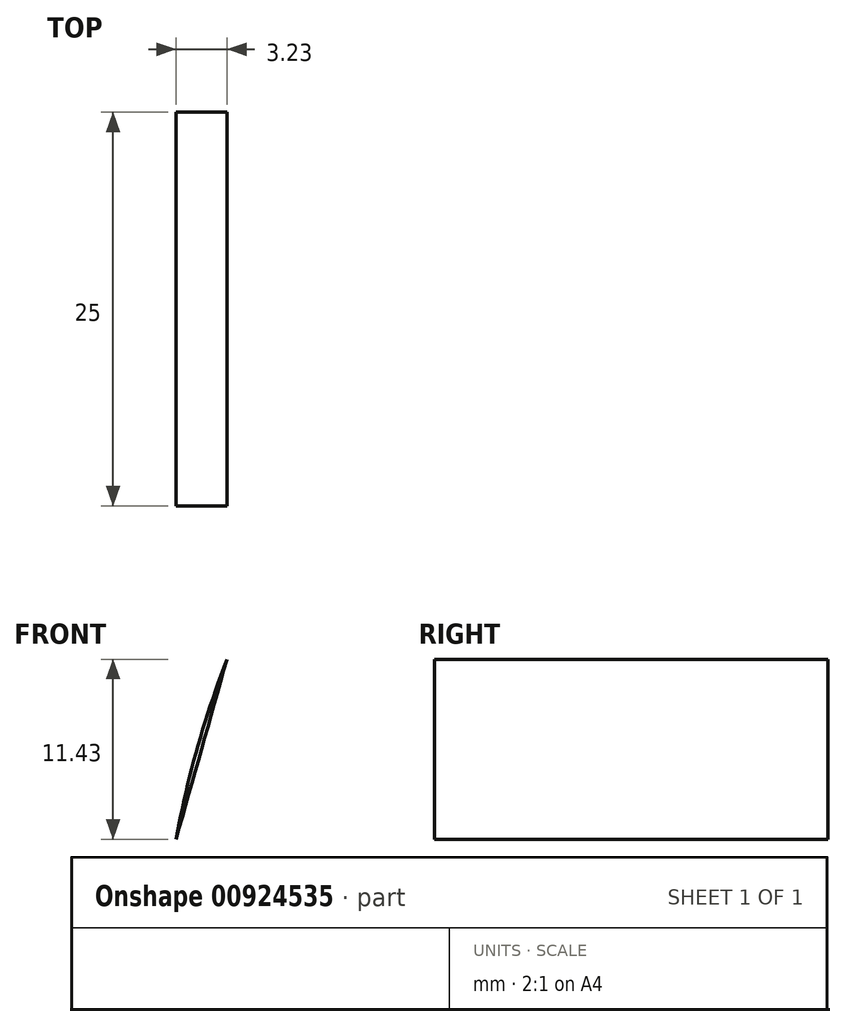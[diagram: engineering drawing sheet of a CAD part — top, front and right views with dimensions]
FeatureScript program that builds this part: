
annotation { "Feature Type Name" : "Feature", "Feature Type Description" : "" }
export const myFeature = defineFeature(function(context is Context, id is Id, definition is map)
    precondition{}
    {
        {
            var Q0;
            Q0=qCreatedBy(makeId("Front.planeOp"),FACE);
            var sketch = newSketch(context, id + "F0", { "sketchPlane" : qUnion([Q0])});
            skLineSegment(sketch, "E0", {"start": v(22.3, 35.3) * mm, "end": v(72.3, 35.3) * mm});
            skLineSegment(sketch, "E1", {"start": v(-23.8, 35.3) * mm, "end": v(-69.1, 35.3) * mm});
            skLineSegment(sketch, "E2", {"start": v(22.3, 35.3) * mm, "end": v(22.3, 55.3) * mm});
            skLineSegment(sketch, "E3", {"start": v(22.3, 55.3) * mm, "end": v(50.7, 55.3) * mm});
            skLineSegment(sketch, "E4", {"start": v(-23.8, 35.3) * mm, "end": v(-23.8, 97.11) * mm});
            skLineSegment(sketch, "E5", {"start": v(-23.8, 97.11) * mm, "end": v(50.7, 55.3) * mm});
            skPoint(sketch, "E6.1.internal.snap0", {"position": v(47.3, 35.3) * mm});
            skPoint(sketch, "E6.2.internal.snap0", {"position": v(47.3, 35.3) * mm});
            skFitSpline(sketch, "E7", {"points": [v(72.3, 35.3) * mm, v(13.13, 169.6) * mm], "startDerivative": vector(113.34, 106.26) * mm, "endDerivative": vector(-178.55, 86.4) * mm});
            skSolve(sketch);
        }
        {
            var Q0;
            Q0=qCreatedBy(makeId("Front.planeOp"),FACE);
            var sketch = newSketch(context, id + "F1", { "sketchPlane" : qUnion([Q0])});
            skFitSpline(sketch, "E8", {"points": [v(-68.82, 35.71) * mm, v(49.25, 199.66) * mm], "startDerivative": vector(0, 92.62) * mm, "endDerivative": vector(464.66, 19.63) * mm});
            skSolve(sketch);
        }
        {
            var Q0;
            Q0=qCreatedBy(makeId("Front.planeOp"),FACE);
            var sketch = newSketch(context, id + "F2", { "sketchPlane" : qUnion([Q0])});
            skFitSpline(sketch, "E9", {"points": [v(49.25, 201.84) * mm, v(0, -110.11) * mm], "startDerivative": vector(-1315.43, -58.9) * mm, "endDerivative": vector(120.58, -137.43) * mm});
            skSolve(sketch);
        }
        {
            var Q0;
            Q0=qCreatedBy(makeId("Front.planeOp"),FACE);
            var sketch = newSketch(context, id + "F3", { "sketchPlane" : qUnion([Q0])});
            skFitSpline(sketch, "E10", {"points": [v(13.09, 169.66) * mm, v(0, -221.1) * mm], "startDerivative": vector(1272.64, -508.97) * mm, "endDerivative": vector(-65.97, -363.39) * mm});
            skFitSpline(sketch, "E11", {"points": [v(0, -110.28) * mm, v(25.23, -30.57) * mm, v(0, -221.1) * mm], "startDerivative": vector(-150, 602.97) * mm, "endDerivative": vector(-133.65, -471.4) * mm});
            skSolve(sketch);
        }
        {
            var Q0;
            Q0 = qSketchRegion(id + "F3", true);
            var Q1;
            Q1 = qSketchRegion(id + "F2", true);
            var Q2;
            Q2 = qSketchRegion(id + "F1", true);
            var Q3;
            Q3 = qSketchRegion(id + "F0", true);
            extrude(context, id + "F4", {"entities" : qUnion([Q0, Q1, Q2, Q3]), "depth" : 25 * mm, "offsetDistance" : 25 * mm});
        }
    });
